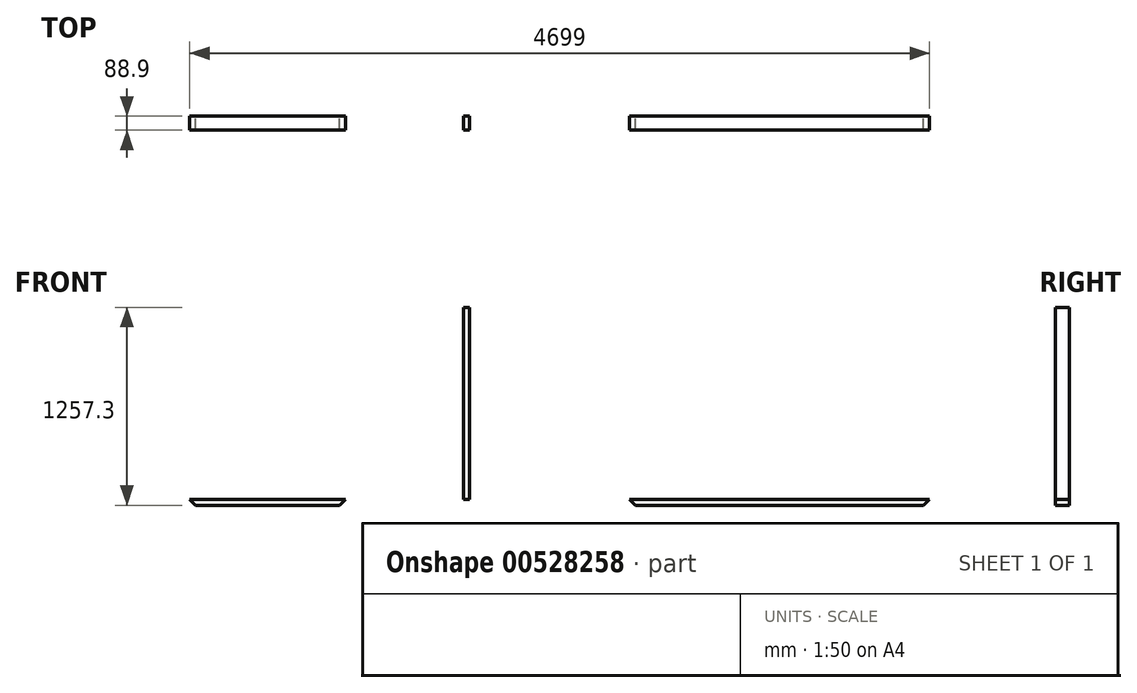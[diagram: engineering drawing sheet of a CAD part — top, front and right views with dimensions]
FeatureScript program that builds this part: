
annotation { "Feature Type Name" : "Feature", "Feature Type Description" : "" }
export const myFeature = defineFeature(function(context is Context, id is Id, definition is map)
    precondition{}
    {
        {
            var Q0;
            Q0=qCreatedBy(makeId("Front.planeOp"),FACE);
            var sketch = newSketch(context, id + "F0", { "sketchPlane" : qUnion([Q0])});
            skLineSegment(sketch, "E0", {"start": v(-1778, 0) * mm, "end": v(-787.4, 0) * mm});
            skLineSegment(sketch, "E1", {"start": v(-787.4, 0) * mm, "end": v(-825.5, -38.1) * mm});
            skLineSegment(sketch, "E2", {"start": v(-825.5, -38.1) * mm, "end": v(-1739.9, -38.1) * mm});
            skLineSegment(sketch, "E3", {"start": v(-1778, 0) * mm, "end": v(-1739.9, -38.1) * mm});
            skSolve(sketch);
        }
        {
            var Q0;
            Q0 = qSketchRegion(id + "F0", true);
            extrude(context, id + "F1", {"entities" : qUnion([Q0]), "depth" : 88.9 * mm, "offsetDistance" : 25.4 * mm});
        }
        {
            var Q0;
            Q0=qCreatedBy(makeId("Front.planeOp"),FACE);
            var sketch = newSketch(context, id + "F2", { "sketchPlane" : qUnion([Q0])});
            skLineSegment(sketch, "E4", {"start": v(-38.1, 1219.2) * mm, "end": v(0, 1219.2) * mm});
            skLineSegment(sketch, "E5", {"start": v(0, 1219.2) * mm, "end": v(0, 0) * mm});
            skLineSegment(sketch, "E6", {"start": v(0, 0) * mm, "end": v(-38.1, 0) * mm});
            skLineSegment(sketch, "E7", {"start": v(-38.1, 0) * mm, "end": v(-38.1, 1219.2) * mm});
            skSolve(sketch);
        }
        {
            var Q0;
            Q0 = qSketchRegion(id + "F2", true);
            extrude(context, id + "F3", {"entities" : qUnion([Q0]), "depth" : 88.9 * mm, "offsetDistance" : 25.4 * mm});
        }
        {
            var Q0;
            Q0=qCreatedBy(makeId("Front.planeOp"),FACE);
            var sketch = newSketch(context, id + "F4", { "sketchPlane" : qUnion([Q0])});
            skLineSegment(sketch, "E8", {"start": v(1016, 0) * mm, "end": v(2921, 0) * mm});
            skLineSegment(sketch, "E9", {"start": v(2882.9, -38.1) * mm, "end": v(2921, 0) * mm});
            skLineSegment(sketch, "E10", {"start": v(2882.9, -38.1) * mm, "end": v(1054.1, -38.1) * mm});
            skLineSegment(sketch, "E11", {"start": v(1054.1, -38.1) * mm, "end": v(1016, 0) * mm});
            skSolve(sketch);
        }
        {
            var Q0;
            Q0 = qSketchRegion(id + "F4", true);
            extrude(context, id + "F5", {"entities" : qUnion([Q0]), "depth" : 88.9 * mm, "offsetDistance" : 25.4 * mm});
        }
    });
